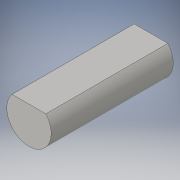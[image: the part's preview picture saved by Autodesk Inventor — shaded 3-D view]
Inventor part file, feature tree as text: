
AUTODESK INVENTOR PART (.ipt)
format: ipt  version: 2016 SP1 (Build 200210100, 210)  size: 86,528 bytes
history: native  units: in
note: dims shown in document units (in); Inventor stores cm internally (conversion verified against a paired STEP export)
features: extrude x1, sketch x1
ambient origin geometry x8: Origin, YZ Plane, XZ Plane, XY Plane, X Axis, Y Axis, Z Axis, Center Point
bodies: Solid1 (feature_tree)
feature tree (2):
  extrude  "Extrusion1"  Depth=0.4331in
  sketch  "Sketch1"  dims[d0=0.1575in d1=0.1299in d2=0.4331in d3=0.0in]
